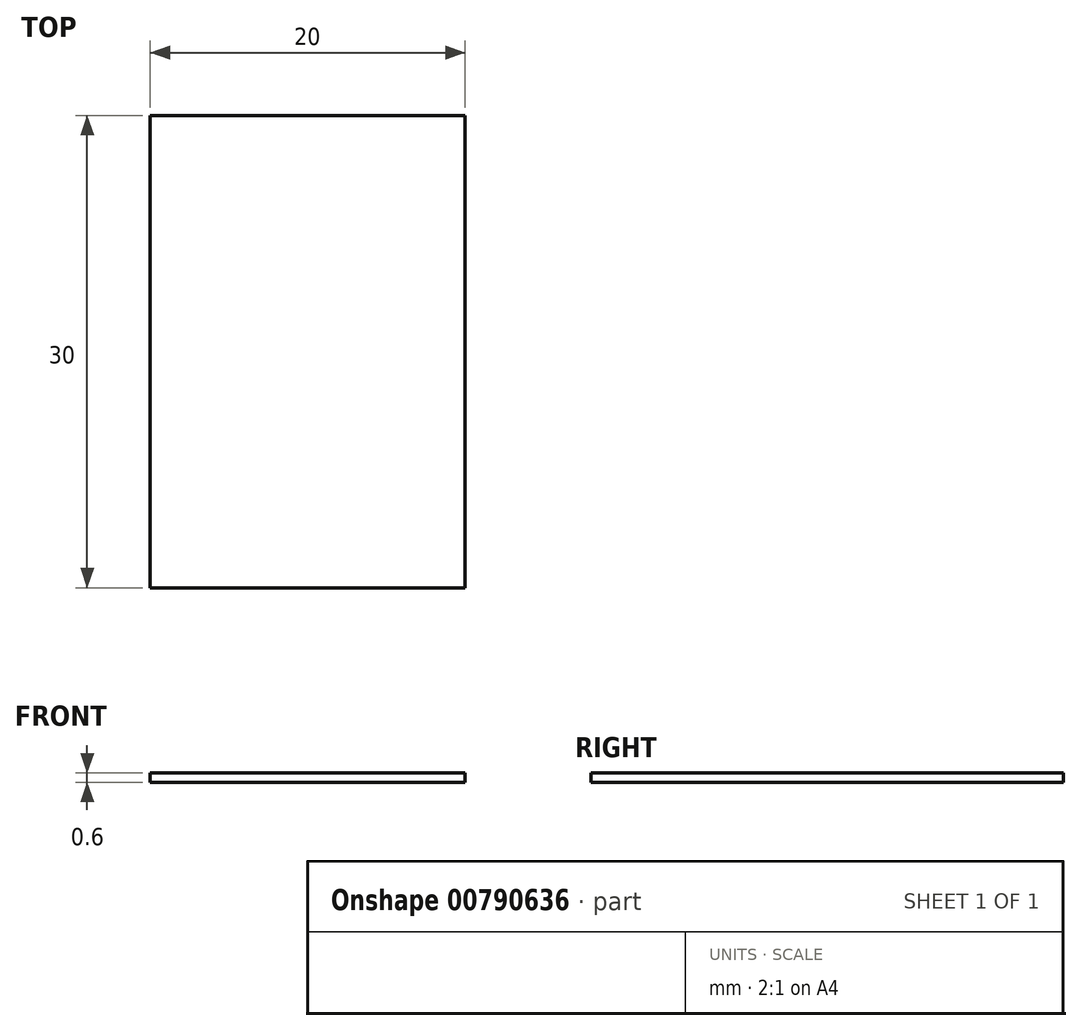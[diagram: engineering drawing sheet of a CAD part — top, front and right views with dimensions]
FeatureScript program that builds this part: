
annotation { "Feature Type Name" : "Feature", "Feature Type Description" : "" }
export const myFeature = defineFeature(function(context is Context, id is Id, definition is map)
    precondition{}
    {
        {
            var Q0;
            Q0=qCreatedBy(makeId("Top.planeOp"),FACE);
            var sketch = newSketch(context, id + "F0", { "sketchPlane" : qUnion([Q0])});
            skLineSegment(sketch, "E0.bottom", {"start": v(0, 0) * mm, "end": v(20, 0) * mm});
            skLineSegment(sketch, "E0.top", {"start": v(0, 30) * mm, "end": v(20, 30) * mm});
            skLineSegment(sketch, "E0.left", {"start": v(0, 0) * mm, "end": v(0, 30) * mm});
            skLineSegment(sketch, "E0.right", {"start": v(20, 0) * mm, "end": v(20, 30) * mm});
            skSolve(sketch);
        }
        {
            var Q0;
            Q0 = qSketchRegion(id + "F0", true);
            extrude(context, id + "F1", {"entities" : qUnion([Q0]), "depth" : 0.6 * mm, "offsetDistance" : 25 * mm});
        }
    });
